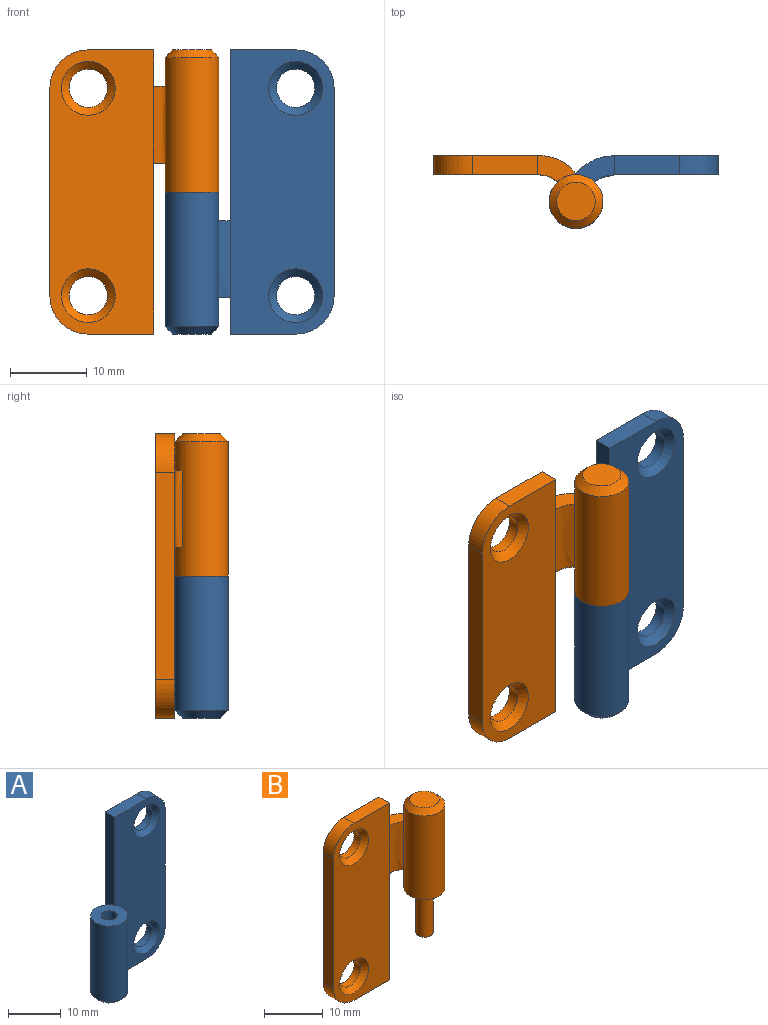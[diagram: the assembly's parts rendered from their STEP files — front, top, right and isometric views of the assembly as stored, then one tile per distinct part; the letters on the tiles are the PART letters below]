
ASSEMBLY  parts=2 mates=1
PART A: 27 faces, bbox 22x9.5x37 mm
  f0: plane 22.25x2.5mm, normal (-1,0,0), area 55.6mm2, adj f5,f9,f10,f26
  f1: plane 8.5x2.5mm, normal (0,0,-1), area 21.2mm2, adj f2,f8,f9,f10
  f2: cylinder r=5mm len=5mm, axis (0,1,0), area 19.6mm2, adj f1,f3,f9,f10
  f3: plane 27x2.5mm, normal (1,0,0), area 67.5mm2, adj f2,f4,f9,f10
  f4: cylinder r=5mm len=5mm, axis (0,1,0), area 19.6mm2, adj f3,f5,f9,f10
  f5: plane 8.5x2.5mm, normal (0,0,1), area 21.2mm2, adj f0,f4,f9,f10
  f6: cylinder r=2.5mm len=5mm, axis (0,1,0), area 23.6mm2, adj f10,f12
  f7: cylinder r=2.5mm len=5mm, axis (0,1,0), area 23.6mm2, adj f10,f11
  f8: plane 4.75x2.5mm, normal (-1,0,0), area 11.9mm2, adj f1,f9,f10,f24
  f9: plane 37x13.5mm, normal (0,-1,0), area 411.8mm2, adj f0,f1,f2,f3,f4,f5,f8,f11
  f10: plane 37x13.5mm, normal (0,1,0), area 449.5mm2, adj f0,f1,f2,f3,f4,f5,f6,f7
  f11: cone r=2.5mm half-angle=45deg, axis (0,-1,0), area 26.7mm2, adj f7,f9
  f12: cone r=2.5mm half-angle=45deg, axis (0,-1,0), area 26.7mm2, adj f6,f9
  f13: cylinder r=3.5mm len=17.5mm, axis (0,0,-1), area 357.1mm2, adj f14,f16,f23,f24,f25,f26
  f14: plane 7x7mm, normal (0,0,1), area 31.4mm2, adj f13,f17
  f15: plane 5x5mm, normal (0,0,-1), area 19.6mm2, adj f16
  f16: cone r=2.5mm half-angle=45deg, axis (0,0,1), area 26.7mm2, adj f13,f15
  f17: cylinder r=1.5mm len=9.25mm, axis (0,0,1), area 70.9mm2, adj f14,f18,f19,f20,f22
  f18: plane 3x2.45mm, normal (0,0,1), area 3.8mm2, adj f17,f19,f20,f21
  f19: bspline ~10x3.47mm, area 5.2mm2, adj f17,f18,f21,f22
  f20: bspline ~10x1.97mm, area 3.9mm2, adj f17,f18,f21,f22
  f21: plane 5.5x2.5mm, normal (0,-1,0), area 13.7mm2, adj f18,f19,f20,f22
  f22: plane 2.57x1.5mm, normal (0,0,1), area 3.2mm2, adj f17,f19,f20,f21
  f23: bspline ~10x6.13mm, area 59.1mm2, adj f10,f13,f24,f26
  f24: plane 5.15x3.45mm, normal (0,0,-1), area 10.4mm2, adj f8,f13,f23,f25
  f25: bspline ~10x3.67mm, area 28.2mm2, adj f9,f13,f24,f26
  f26: plane 5.15x3.45mm, normal (0,0,1), area 10.4mm2, adj f0,f13,f23,f25
PART B: 23 faces, bbox 22x9.5x37 mm
  f0: cylinder r=3.5mm len=17.5mm, axis (0,0,1), area 357.7mm2, adj f1,f3,f6,f7,f8,f9
  f1: plane 7x7mm, normal (0,0,-1), area 31.4mm2, adj f0,f4
  f2: plane 5x5mm, normal (0,0,1), area 19.6mm2, adj f3
  f3: cone r=3.5mm half-angle=45deg, axis (0,0,-1), area 26.7mm2, adj f0,f2
  f4: cylinder r=1.5mm len=9.25mm, axis (0,0,1), area 87.2mm2, adj f1,f5
  f5: plane 3x3mm, normal (0,0,-1), area 7.1mm2, adj f4
  f6: bspline ~10x3.36mm, area 28.3mm2, adj f0,f8,f9,f19
  f7: bspline ~10x6.13mm, area 58.7mm2, adj f0,f8,f9,f20
  f8: plane 5.08x3.47mm, normal (0,0,-1), area 10.4mm2, adj f0,f6,f7,f11
  f9: plane 5.08x3.47mm, normal (0,0,1), area 10.4mm2, adj f0,f6,f7,f10
  f10: plane 4.75x2.5mm, normal (1,0,0), area 11.9mm2, adj f9,f15,f19,f20
  f11: plane 22.25x2.5mm, normal (1,0,0), area 55.6mm2, adj f8,f14,f19,f20
  f12: plane 27x2.5mm, normal (-1,0,0), area 67.5mm2, adj f13,f18,f19,f20
  f13: cylinder r=5mm len=5mm, axis (0,1,0), area 19.6mm2, adj f12,f14,f19,f20
  f14: plane 8.5x2.5mm, normal (0,0,-1), area 21.2mm2, adj f11,f13,f19,f20
  f15: plane 8.5x2.5mm, normal (0,0,1), area 21.2mm2, adj f10,f18,f19,f20
  f16: cylinder r=2.5mm len=5mm, axis (0,1,0), area 23.6mm2, adj f20,f21
  f17: cylinder r=2.5mm len=5mm, axis (0,1,0), area 23.6mm2, adj f20,f22
  f18: cylinder r=5mm len=5mm, axis (0,1,0), area 19.6mm2, adj f12,f15,f19,f20
  f19: plane 37x13.5mm, normal (0,-1,0), area 411.8mm2, adj f6,f10,f11,f12,f13,f14,f15,f18
  f20: plane 37x13.5mm, normal (0,1,0), area 449.5mm2, adj f7,f10,f11,f12,f13,f14,f15,f16
  f21: cone r=2.5mm half-angle=45deg, axis (0,-1,0), area 26.7mm2, adj f16,f19
  f22: cone r=2.5mm half-angle=45deg, axis (0,-1,0), area 26.7mm2, adj f17,f19
PLACE A rot(axis=(0,0,-1),0deg) t=(-0.93,3.26,-0.61)mm fixed
PLACE B rot(axis=(0,0,1),0deg) t=(-0.93,3.26,-0.61)mm
MATE revolute B.f4 <-> A.f17  axis (0,0,-1) through (-0.93,-2.74,-9.86)mm
